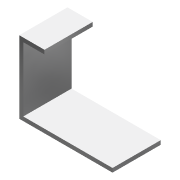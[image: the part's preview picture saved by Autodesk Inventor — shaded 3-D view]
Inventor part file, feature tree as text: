
AUTODESK INVENTOR PART (.ipt)
format: ipt  version: 2014 (Build 180170000, 170)  size: 82,432 bytes
history: native  units: in
note: dims shown in document units (in); Inventor stores cm internally (conversion verified against a paired STEP export)
features: extrude x2, sketch x2
ambient origin geometry x8: Origin, YZ Plane, XZ Plane, XY Plane, X Axis, Y Axis, Z Axis, Center Point
bodies: Solid1 (feature_tree)
feature tree (4):
  extrude  "Extrusion1"  Depth=0.12in TaperAngle=0.0deg
  extrude  "Extrusion2"  Depth=0.01in
  sketch  "Sketch1"  dims[d1=0.01in d2=0.12in d3=0.0in]
  sketch  "Sketch2"  dims[d4=0.222in d5=0.01in d6=0.12in d7=0.0in d8=0.18in]
